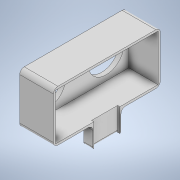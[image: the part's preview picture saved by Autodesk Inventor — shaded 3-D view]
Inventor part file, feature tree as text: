
AUTODESK INVENTOR PART (.ipt)
format: ipt  version: 2021 (Build 250183000, 183)  size: 196,608 bytes
history: native  units: in
note: dims shown in document units (in); Inventor stores cm internally (conversion verified against a paired STEP export)
features: extrude x6, sketch x4, fillet x4, projected_geometry x2
ambient origin geometry x8: Origin, YZ Plane, XZ Plane, XY Plane, X Axis, Y Axis, Z Axis, Center Point
bodies: Solid1 (feature_tree)
feature tree (16):
  sketch  "Sketch1"  dims[d12=0.5906in d13=0.0in d14=0.0394in]
  extrude  "Extrusion1"  Depth=0.0394in
  extrude  "Extrusion2"  Depth=0.5118in TaperAngle=0.0deg
  extrude  "Extrusion3"  Depth=0.6496in
  extrude  "Extrusion4"  Depth=0.374in
  extrude  "Extrusion5"  Depth=0.0394in
  extrude  "Extrusion6"  Depth=0.4961in
  fillet  "Fillet1"  Radius=0.1575in
  fillet  "Fillet2"  Radius=0.0197in
  fillet  "Fillet3"  Radius=0.0394in
  fillet  "Fillet4"  Radius=0.0787in
  sketch  "Sketch2"  dims[d15=0.4331in d16=0.0in d17=0.5118in d18=0.0in]
  sketch  "Sketch3"  dims[d19=0.4331in d20=0.0in d21=0.6496in]
  projected_geometry  "Projected Loop1"
  sketch  "Sketch4"  dims[d22=0.6496in d23=0.374in d24=0.0394in d26=0.4961in d27=0.1575in d28=0.0in d29=0.0197in d30=0.0394in d31=0.0in d32=0.0787in d33=0.0787in d34=0.0394in d35=0.0394in]
  projected_geometry  "Projected Loop2"
